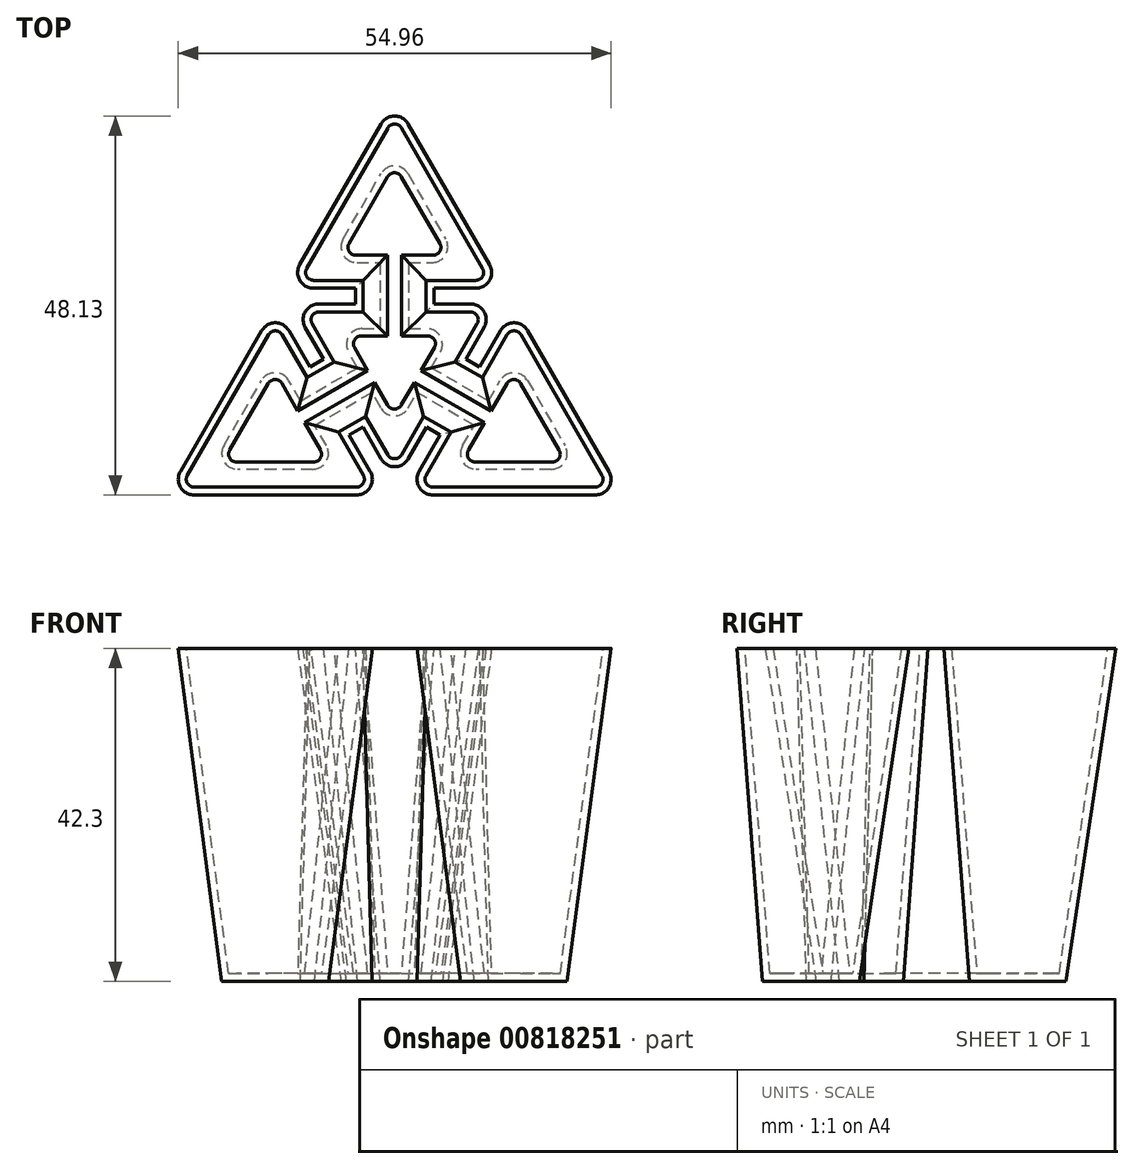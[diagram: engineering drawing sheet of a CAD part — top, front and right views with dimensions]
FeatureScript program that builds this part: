
annotation { "Feature Type Name" : "Feature", "Feature Type Description" : "" }
export const myFeature = defineFeature(function(context is Context, id is Id, definition is map)
    precondition{}
    {
        {
            var Q0;
            Q0=qCreatedBy(makeId("Top.planeOp"),FACE);
            var sketch = newSketch(context, id + "F0", { "sketchPlane" : qUnion([Q0])});
            skLineSegment(sketch, "E0", {"start": v(-1.39, -16.7) * mm, "end": v(-5.77, -9.1) * mm});
            skLineSegment(sketch, "E1", {"start": v(1.39, -16.7) * mm, "end": v(5.77, -9.1) * mm});
            skLineSegment(sketch, "E2", {"start": v(-13.78, 9.55) * mm, "end": v(-5, 9.55) * mm});
            skPoint(sketch, "E3.cCircle.center.orphan", {"position": v(0, 0) * mm});
            skLineSegment(sketch, "E4.1", {"start": v(0, -15.1) * mm, "end": v(-4.04, -8.1) * mm});
            skLineSegment(sketch, "E4.2", {"start": v(0, -15.1) * mm, "end": v(4.04, -8.1) * mm});
            skLineSegment(sketch, "E5.0", {"start": v(-5.77, -9.1) * mm, "end": v(-4.04, -8.1) * mm});
            skLineSegment(sketch, "E6.0", {"start": v(-10.77, -0.45) * mm, "end": v(-9.04, 0.55) * mm});
            skLineSegment(sketch, "E7.0", {"start": v(10.77, -0.45) * mm, "end": v(9.04, 0.55) * mm});
            skLineSegment(sketch, "E8.0", {"start": v(5.77, -9.1) * mm, "end": v(4.04, -8.1) * mm});
            skLineSegment(sketch, "E9.0", {"start": v(-5, 9.55) * mm, "end": v(-5, 7.55) * mm});
            skLineSegment(sketch, "E10.0", {"start": v(5, 9.55) * mm, "end": v(5, 7.55) * mm});
            skLineSegment(sketch, "E11.0", {"start": v(-28.94, -16.7) * mm, "end": v(-15.16, 7.15) * mm});
            skLineSegment(sketch, "E11.1", {"start": v(28.94, -16.7) * mm, "end": v(1.39, -16.7) * mm});
            skLineSegment(sketch, "E11.2", {"start": v(0, 33.42) * mm, "end": v(13.78, 9.55) * mm});
            skLineSegment(sketch, "E12.trimOffspring", {"start": v(-13.78, 9.55) * mm, "end": v(0, 33.42) * mm});
            skLineSegment(sketch, "E13.trimOffspring", {"start": v(15.16, 7.15) * mm, "end": v(28.94, -16.7) * mm});
            skLineSegment(sketch, "E14.trimOffspring", {"start": v(-1.39, -16.7) * mm, "end": v(-28.94, -16.7) * mm});
            skLineSegment(sketch, "E15.trimOffspring", {"start": v(-9.04, 0.55) * mm, "end": v(-13.08, 7.55) * mm});
            skLineSegment(sketch, "E16.trimOffspring", {"start": v(-10.77, -0.45) * mm, "end": v(-15.16, 7.15) * mm});
            skLineSegment(sketch, "E17.trimOffspring", {"start": v(5, 9.55) * mm, "end": v(13.78, 9.55) * mm});
            skLineSegment(sketch, "E18.trimOffspring", {"start": v(5, 7.55) * mm, "end": v(13.08, 7.55) * mm});
            skLineSegment(sketch, "E19.trimOffspring", {"start": v(9.04, 0.55) * mm, "end": v(13.08, 7.55) * mm});
            skLineSegment(sketch, "E20.trimOffspring", {"start": v(10.77, -0.45) * mm, "end": v(15.16, 7.15) * mm});
            skLineSegment(sketch, "E21", {"start": v(-13.08, 7.55) * mm, "end": v(-5, 7.55) * mm});
            skLineSegment(sketch, "E22.0", {"start": v(-8.23, 12.75) * mm, "end": v(0, 27.02) * mm});
            skLineSegment(sketch, "E22.1", {"start": v(0, -8.7) * mm, "end": v(-2.87, -3.74) * mm});
            skLineSegment(sketch, "E22.2", {"start": v(-10.15, -7.94) * mm, "end": v(-2.87, -3.74) * mm});
            skLineSegment(sketch, "E22.3", {"start": v(-6.93, -13.5) * mm, "end": v(-10.15, -7.94) * mm});
            skLineSegment(sketch, "E22.4", {"start": v(-6.93, -13.5) * mm, "end": v(-23.4, -13.5) * mm});
            skLineSegment(sketch, "E22.5", {"start": v(-23.4, -13.5) * mm, "end": v(-15.16, 0.75) * mm});
            skLineSegment(sketch, "E22.6", {"start": v(-11.95, -4.82) * mm, "end": v(-15.16, 0.75) * mm});
            skLineSegment(sketch, "E22.7", {"start": v(-1.8, 12.75) * mm, "end": v(-1.8, 4.35) * mm});
            skLineSegment(sketch, "E22.8", {"start": v(-7.54, 4.35) * mm, "end": v(-1.8, 4.35) * mm});
            skLineSegment(sketch, "E22.9", {"start": v(-4.67, -0.62) * mm, "end": v(-7.54, 4.35) * mm});
            skLineSegment(sketch, "E22.10", {"start": v(-11.95, -4.82) * mm, "end": v(-4.67, -0.62) * mm});
            skLineSegment(sketch, "E22.11", {"start": v(0, -8.7) * mm, "end": v(2.87, -3.74) * mm});
            skLineSegment(sketch, "E22.12", {"start": v(-8.23, 12.75) * mm, "end": v(-1.8, 12.75) * mm});
            skLineSegment(sketch, "E22.13", {"start": v(10.15, -7.94) * mm, "end": v(2.87, -3.74) * mm});
            skLineSegment(sketch, "E22.14", {"start": v(6.93, -13.5) * mm, "end": v(10.15, -7.94) * mm});
            skLineSegment(sketch, "E22.15", {"start": v(23.4, -13.5) * mm, "end": v(6.93, -13.5) * mm});
            skLineSegment(sketch, "E22.16", {"start": v(15.16, 0.75) * mm, "end": v(23.4, -13.5) * mm});
            skLineSegment(sketch, "E22.17", {"start": v(11.95, -4.82) * mm, "end": v(15.16, 0.75) * mm});
            skLineSegment(sketch, "E22.18", {"start": v(11.95, -4.82) * mm, "end": v(4.67, -0.62) * mm});
            skLineSegment(sketch, "E22.19", {"start": v(4.67, -0.62) * mm, "end": v(7.54, 4.35) * mm});
            skLineSegment(sketch, "E22.20", {"start": v(1.8, 4.35) * mm, "end": v(7.54, 4.35) * mm});
            skLineSegment(sketch, "E22.21", {"start": v(1.8, 12.75) * mm, "end": v(1.8, 4.35) * mm});
            skLineSegment(sketch, "E22.22", {"start": v(1.8, 12.75) * mm, "end": v(8.23, 12.75) * mm});
            skLineSegment(sketch, "E22.23", {"start": v(0, 27.02) * mm, "end": v(8.23, 12.75) * mm});
            skSolve(sketch);
        }
        {
            var Q0;
            Q0=qCreatedBy(makeId("Top.planeOp"),FACE);
            cPlane(context, id + "F1", {"entities" : qUnion([Q0]), "cplaneType" : CPlaneType.OFFSET, "offset" : 42.3 * mm, "width" : 150 * mm, "height" : 150 * mm});
        }
        {
            var Q0;
            Q0=qCreatedBy(id+"F1.planeOp",FACE);
            var sketch = newSketch(context, id + "F2", { "sketchPlane" : qUnion([Q0])});
            skLineSegment(sketch, "E23", {"start": v(-1.36, -16.77) * mm, "end": v(-5.74, -9.17) * mm});
            skLineSegment(sketch, "E24", {"start": v(1.42, -16.77) * mm, "end": v(5.8, -9.17) * mm});
            skLineSegment(sketch, "E25", {"start": v(-13.75, 9.5) * mm, "end": v(-4.97, 9.5) * mm});
            skPoint(sketch, "E26.cCircle.center.orphan", {"position": v(0.03, -0.06) * mm});
            skLineSegment(sketch, "E27.1", {"start": v(0.03, -15.17) * mm, "end": v(-4.01, -8.17) * mm});
            skLineSegment(sketch, "E27.2", {"start": v(0.03, -15.17) * mm, "end": v(4.07, -8.17) * mm});
            skLineSegment(sketch, "E28.0", {"start": v(-5.74, -9.17) * mm, "end": v(-4.01, -8.17) * mm});
            skLineSegment(sketch, "E29.0", {"start": v(-10.74, -0.5) * mm, "end": v(-9.01, 0.5) * mm});
            skLineSegment(sketch, "E30.0", {"start": v(10.8, -0.5) * mm, "end": v(9.07, 0.5) * mm});
            skLineSegment(sketch, "E31.0", {"start": v(5.8, -9.17) * mm, "end": v(4.07, -8.17) * mm});
            skLineSegment(sketch, "E32.0", {"start": v(-4.97, 9.5) * mm, "end": v(-4.97, 7.5) * mm});
            skLineSegment(sketch, "E33.0", {"start": v(5.03, 9.5) * mm, "end": v(5.03, 7.5) * mm});
            skLineSegment(sketch, "E34.0", {"start": v(-28.9, -16.77) * mm, "end": v(-15.13, 7.1) * mm});
            skLineSegment(sketch, "E34.1", {"start": v(28.97, -16.77) * mm, "end": v(1.42, -16.77) * mm});
            skLineSegment(sketch, "E34.2", {"start": v(0.03, 33.35) * mm, "end": v(13.8, 9.5) * mm});
            skLineSegment(sketch, "E35.trimOffspring", {"start": v(-13.75, 9.5) * mm, "end": v(0.03, 33.35) * mm});
            skLineSegment(sketch, "E36.trimOffspring", {"start": v(15.2, 7.1) * mm, "end": v(28.97, -16.77) * mm});
            skLineSegment(sketch, "E37.trimOffspring", {"start": v(-1.36, -16.77) * mm, "end": v(-28.9, -16.77) * mm});
            skLineSegment(sketch, "E38.trimOffspring", {"start": v(-9.01, 0.5) * mm, "end": v(-13.05, 7.5) * mm});
            skLineSegment(sketch, "E39.trimOffspring", {"start": v(-10.74, -0.5) * mm, "end": v(-15.13, 7.1) * mm});
            skLineSegment(sketch, "E40.trimOffspring", {"start": v(5.03, 9.5) * mm, "end": v(13.8, 9.5) * mm});
            skLineSegment(sketch, "E41.trimOffspring", {"start": v(5.03, 7.5) * mm, "end": v(13.11, 7.5) * mm});
            skLineSegment(sketch, "E42.trimOffspring", {"start": v(9.07, 0.5) * mm, "end": v(13.11, 7.5) * mm});
            skLineSegment(sketch, "E43.trimOffspring", {"start": v(10.8, -0.5) * mm, "end": v(15.2, 7.1) * mm});
            skLineSegment(sketch, "E44", {"start": v(-13.05, 7.5) * mm, "end": v(-4.97, 7.5) * mm});
            skSolve(sketch);
        }
        {
            var Q0;
            Q0=makeQuery(id+"F0.imprint","IMPRINT",FACE,{"disambiguationData":[TD([[makeQuery(id+"F0.imprint","IMPRINT",EDGE,{"derivedFrom":sQuery(id+"F0.wireOp",EDGE,"E22.0")}),-1.0]])]});
            var Q1;
            Q1=makeQuery(id+"F2.imprint","IMPRINT",FACE,{"disambiguationData":[TD([[makeQuery(id+"F2.imprint","IMPRINT",EDGE,{"derivedFrom":sQuery(id+"F2.wireOp",EDGE,"E23")}),1.0]])]});
            loft(context, id + "F3", {"sheetProfilesArray" : [{ "sheetProfileEntities" : qUnion([Q0]) }, { "sheetProfileEntities" : qUnion([Q1]) }]});
        }
        {
            var Q0;
            Q0=makeQuery(id+"F3.opLoft","SWEPT_EDGE",EDGE,{"disambiguationData":[OSD([sQuery(id+"F0.wireOp",EDGE,"E22.4"),sQuery(id+"F0.wireOp",EDGE,"E22.5"),sQuery(id+"F2.wireOp",EDGE,"E34.0"),sQuery(id+"F2.wireOp",EDGE,"E37.trimOffspring")])]});
            var Q1;
            Q1=makeQuery(id+"F3.opLoft","SWEPT_EDGE",EDGE,{"disambiguationData":[OSD([sQuery(id+"F0.wireOp",EDGE,"E22.15"),sQuery(id+"F0.wireOp",EDGE,"E22.16"),sQuery(id+"F2.wireOp",EDGE,"E34.1"),sQuery(id+"F2.wireOp",EDGE,"E36.trimOffspring")])]});
            var Q2;
            Q2=makeQuery(id+"F3.opLoft","SWEPT_EDGE",EDGE,{"disambiguationData":[OSD([sQuery(id+"F0.wireOp",EDGE,"E22.0"),sQuery(id+"F0.wireOp",EDGE,"E22.23"),sQuery(id+"F2.wireOp",EDGE,"E34.2"),sQuery(id+"F2.wireOp",EDGE,"E35.trimOffspring")])]});
            var Q3;
            Q3=makeQuery(id+"F3.opLoft","SWEPT_EDGE",EDGE,{"disambiguationData":[OSD([sQuery(id+"F0.wireOp",EDGE,"E22.16"),sQuery(id+"F0.wireOp",EDGE,"E22.17"),sQuery(id+"F2.wireOp",EDGE,"E36.trimOffspring"),sQuery(id+"F2.wireOp",EDGE,"E43.trimOffspring")])]});
            var Q4;
            Q4=makeQuery(id+"F3.opLoft","SWEPT_EDGE",EDGE,{"disambiguationData":[OSD([sQuery(id+"F0.wireOp",EDGE,"E22.22"),sQuery(id+"F0.wireOp",EDGE,"E22.23"),sQuery(id+"F2.wireOp",EDGE,"E34.2"),sQuery(id+"F2.wireOp",EDGE,"E40.trimOffspring")])]});
            var Q5;
            Q5=makeQuery(id+"F3.opLoft","SWEPT_EDGE",EDGE,{"disambiguationData":[OSD([sQuery(id+"F0.wireOp",EDGE,"E22.0"),sQuery(id+"F0.wireOp",EDGE,"E22.12"),sQuery(id+"F2.wireOp",EDGE,"E25"),sQuery(id+"F2.wireOp",EDGE,"E35.trimOffspring")])]});
            var Q6;
            Q6=makeQuery(id+"F3.opLoft","SWEPT_EDGE",EDGE,{"disambiguationData":[OSD([sQuery(id+"F0.wireOp",EDGE,"E22.5"),sQuery(id+"F0.wireOp",EDGE,"E22.6"),sQuery(id+"F2.wireOp",EDGE,"E34.0"),sQuery(id+"F2.wireOp",EDGE,"E39.trimOffspring")])]});
            var Q7;
            Q7=makeQuery(id+"F3.opLoft","SWEPT_EDGE",EDGE,{"disambiguationData":[OSD([sQuery(id+"F0.wireOp",EDGE,"E22.14"),sQuery(id+"F0.wireOp",EDGE,"E22.15"),sQuery(id+"F2.wireOp",EDGE,"E24"),sQuery(id+"F2.wireOp",EDGE,"E34.1")])]});
            var Q8;
            Q8=makeQuery(id+"F3.opLoft","SWEPT_EDGE",EDGE,{"disambiguationData":[OSD([sQuery(id+"F0.wireOp",EDGE,"E22.3"),sQuery(id+"F0.wireOp",EDGE,"E22.4"),sQuery(id+"F2.wireOp",EDGE,"E23"),sQuery(id+"F2.wireOp",EDGE,"E37.trimOffspring")])]});
            var Q9;
            Q9=makeQuery(id+"F3.opLoft","SWEPT_EDGE",EDGE,{"disambiguationData":[OSD([sQuery(id+"F0.wireOp",EDGE,"E22.8"),sQuery(id+"F0.wireOp",EDGE,"E22.9"),sQuery(id+"F2.wireOp",EDGE,"E38.trimOffspring"),sQuery(id+"F2.wireOp",EDGE,"E44")])]});
            var Q10;
            Q10=makeQuery(id+"F3.opLoft","SWEPT_EDGE",EDGE,{"disambiguationData":[OSD([sQuery(id+"F0.wireOp",EDGE,"E22.1"),sQuery(id+"F0.wireOp",EDGE,"E22.11"),sQuery(id+"F2.wireOp",EDGE,"E27.1"),sQuery(id+"F2.wireOp",EDGE,"E27.2")])]});
            var Q11;
            Q11=makeQuery(id+"F3.opLoft","SWEPT_EDGE",EDGE,{"disambiguationData":[OSD([sQuery(id+"F0.wireOp",EDGE,"E22.19"),sQuery(id+"F0.wireOp",EDGE,"E22.20"),sQuery(id+"F2.wireOp",EDGE,"E41.trimOffspring"),sQuery(id+"F2.wireOp",EDGE,"E42.trimOffspring")])]});
            fillet(context, id + "F4", {"entities" : qUnion([Q0, Q1, Q2, Q3, Q4, Q5, Q6, Q7, Q8, Q9, Q10, Q11]), "radius" : 2 * mm, "tangentPropagation" : true, "allowEdgeOverflow" : false});
        }
        {
            var Q0;
            Q0=makeQuery(id+"F3.opLoft","CAP_FACE",FACE,{"disambiguationData":[OSD([makeQuery(id+"F2.imprint","IMPRINT",FACE,{"disambiguationData":[TD([[makeQuery(id+"F2.imprint","IMPRINT",EDGE,{"derivedFrom":sQuery(id+"F2.wireOp",EDGE,"E23")}),1.0]])]})])],"isStart":true});
            shell(context, id + "F5", {"entities" : qUnion([Q0]), "thickness" : 1 * mm});
        }
    });
